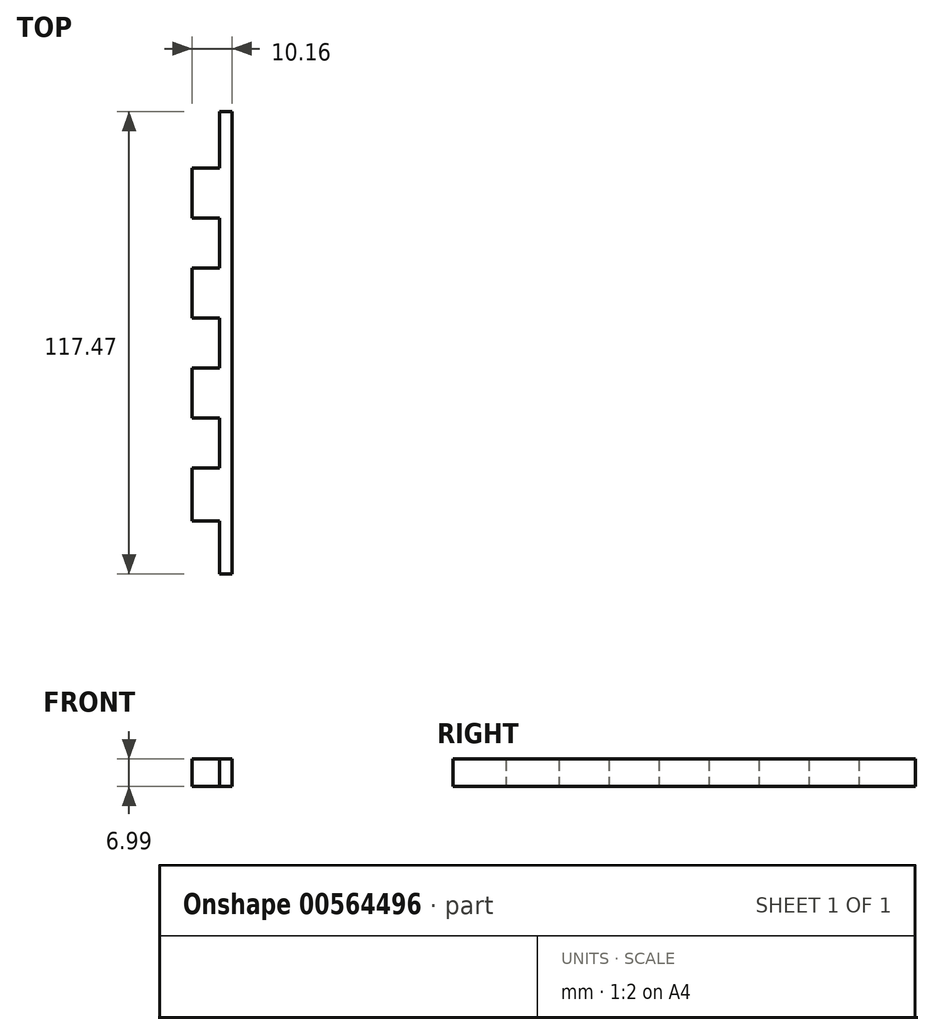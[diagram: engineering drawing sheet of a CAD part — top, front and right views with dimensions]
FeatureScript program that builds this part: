
annotation { "Feature Type Name" : "Feature", "Feature Type Description" : "" }
export const myFeature = defineFeature(function(context is Context, id is Id, definition is map)
    precondition{}
    {
        {
            var Q0;
            Q0=qCreatedBy(makeId("Top.planeOp"),FACE);
            var sketch = newSketch(context, id + "F0", { "sketchPlane" : qUnion([Q0])});
            skLineSegment(sketch, "E0.bottom", {"start": v(6.99, 0) * mm, "end": v(10.16, 0) * mm});
            skLineSegment(sketch, "E0.top", {"start": v(6.99, -117.48) * mm, "end": v(10.16, -117.48) * mm});
            skLineSegment(sketch, "E0.left", {"start": v(0, -14.3) * mm, "end": v(0, -27) * mm});
            skLineSegment(sketch, "E0.right", {"start": v(10.16, 0) * mm, "end": v(10.16, -117.48) * mm});
            skLineSegment(sketch, "E1", {"start": v(0, -14.3) * mm, "end": v(6.99, -14.3) * mm});
            skLineSegment(sketch, "E2", {"start": v(6.99, -14.3) * mm, "end": v(6.99, 0) * mm});
            skLineSegment(sketch, "E3", {"start": v(0, -27) * mm, "end": v(6.99, -27) * mm});
            skLineSegment(sketch, "E4", {"start": v(6.99, -27) * mm, "end": v(6.99, -39.7) * mm});
            skLineSegment(sketch, "E5", {"start": v(6.99, -39.7) * mm, "end": v(0, -39.7) * mm});
            skLineSegment(sketch, "E6", {"start": v(0, -39.7) * mm, "end": v(0, -52.4) * mm});
            skLineSegment(sketch, "E7", {"start": v(0, -52.4) * mm, "end": v(6.99, -52.4) * mm});
            skLineSegment(sketch, "E8", {"start": v(6.99, -52.4) * mm, "end": v(6.99, -65.1) * mm});
            skLineSegment(sketch, "E9", {"start": v(6.99, -65.1) * mm, "end": v(0, -65.1) * mm});
            skLineSegment(sketch, "E10", {"start": v(0, -65.1) * mm, "end": v(0, -77.8) * mm});
            skLineSegment(sketch, "E11", {"start": v(0, -77.8) * mm, "end": v(6.99, -77.8) * mm});
            skLineSegment(sketch, "E12", {"start": v(6.99, -77.8) * mm, "end": v(6.99, -90.5) * mm});
            skLineSegment(sketch, "E13", {"start": v(6.99, -90.5) * mm, "end": v(0, -90.5) * mm});
            skPoint(sketch, "E14.orphan", {"position": v(0, 0) * mm});
            skLineSegment(sketch, "E15.trimOffspring", {"start": v(0, -90.5) * mm, "end": v(0, -103.99) * mm});
            skLineSegment(sketch, "E16", {"start": v(0, -103.99) * mm, "end": v(6.99, -103.99) * mm});
            skLineSegment(sketch, "E17", {"start": v(6.99, -103.99) * mm, "end": v(6.99, -117.48) * mm});
            skPoint(sketch, "E18.orphan", {"position": v(0, -117.48) * mm});
            skSolve(sketch);
        }
        {
            var Q0;
            Q0=makeQuery(id+"F0.imprint","IMPRINT",FACE,{"disambiguationData":[TD([[makeQuery(id+"F0.imprint","IMPRINT",EDGE,{"derivedFrom":sQuery(id+"F0.wireOp",EDGE,"E0.bottom")}),-1.0]])]});
            extrude(context, id + "F1", {"entities" : qUnion([Q0]), "depth" : 7 * mm, "offsetDistance" : 25.4 * mm});
        }
    });
